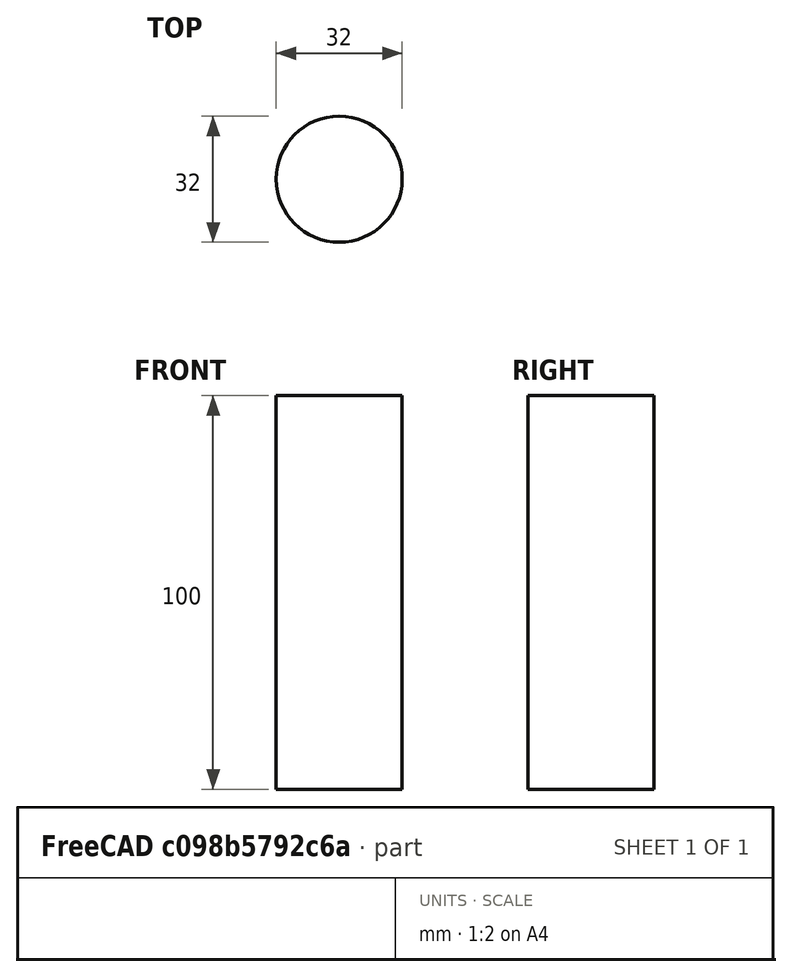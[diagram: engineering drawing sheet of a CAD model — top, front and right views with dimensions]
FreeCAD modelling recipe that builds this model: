
FCSTD DOCUMENT  (FreeCAD 1.0R39109 (Git))
Label: power_bank
License: All rights reserved
LicenseURL: https://en.wikipedia.org/wiki/All_rights_reserved
objects: Sketcher::SketchObject×1, PartDesign::Pad×1, PartDesign::Body×1
note: 6 computed .brp shape members not serialized (recipe doc carries the construction recipe); baked Part::Feature solids carry a one-line shape summary decoded from their .brp

FEATURE [Sketcher::SketchObject] Sketch
  ArcFitTolerance = 1e-06
  AttachmentSupport = -> [XY_Plane]
  FullyConstrained = false
  MakeInternals = false
  MapMode = 5
  sketch-geometry (1):
    g0: Circle CenterX=-270.885 CenterY=-152.032 CenterZ=0 NormalX=0 NormalY=0 NormalZ=1 AngleXU=0 Radius=16
  constraints (1):
    c: Diameter(g0) = 32
FEATURE [PartDesign::Pad] Pad
  Direction = (0,0,1)
  Length = 100
  Length2 = 10
  Profile = -> Sketch
  ReferenceAxis = -> Sketch [N_Axis]
  Refine = true
  Suppressed = false
  Type = 0
FEATURE [PartDesign::Body] Body
  AllowCompound = false
  Group = -> [Sketch,Pad]
  Origin = -> Origin
  Tip = -> Pad
